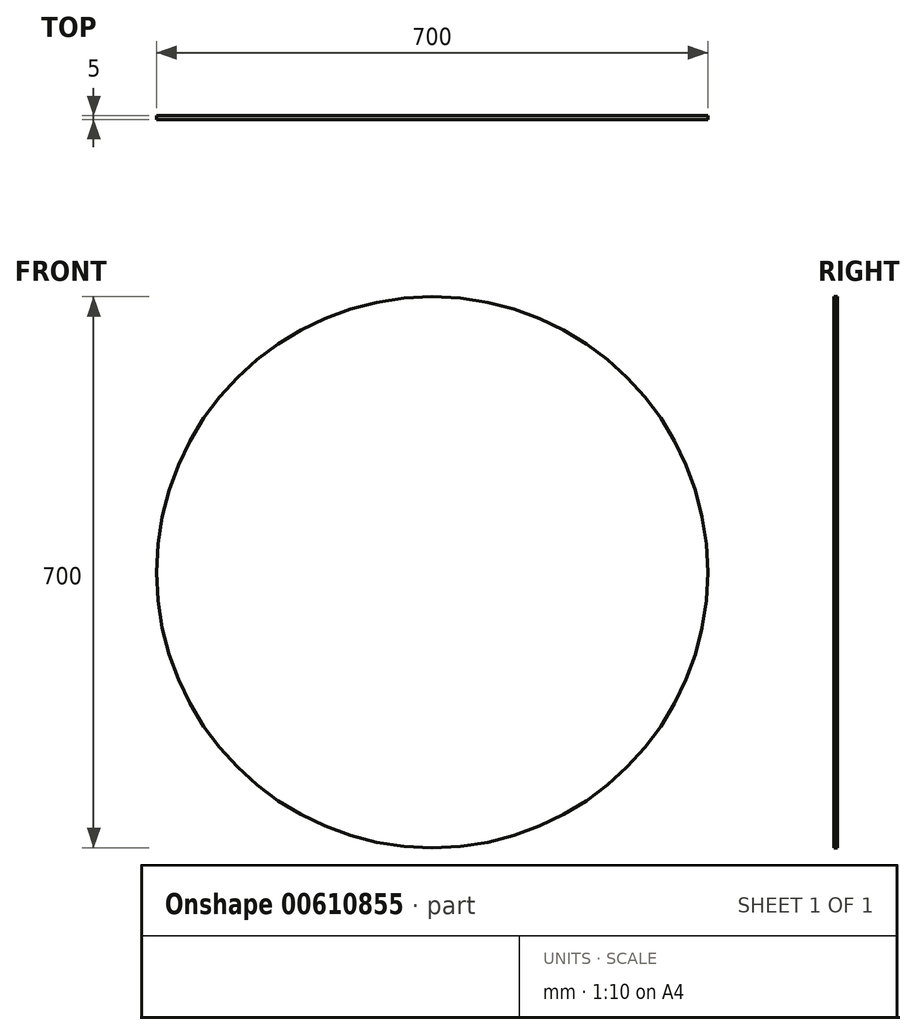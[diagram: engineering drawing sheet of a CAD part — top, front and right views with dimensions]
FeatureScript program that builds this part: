
annotation { "Feature Type Name" : "Feature", "Feature Type Description" : "" }
export const myFeature = defineFeature(function(context is Context, id is Id, definition is map)
    precondition{}
    {
        {
            var Q0;
            Q0=qCreatedBy(makeId("Front.planeOp"),FACE);
            var sketch = newSketch(context, id + "F0", { "sketchPlane" : qUnion([Q0])});
            skCircle(sketch, "E0", {"center": v(0, 0) * mm, "radius": 350 * mm});
            skSolve(sketch);
        }
        {
            var Q0;
            Q0 = qSketchRegion(id + "F0", true);
            extrude(context, id + "F1", {"entities" : qUnion([Q0]), "depth" : 5 * mm, "offsetDistance" : 25 * mm});
        }
    });
